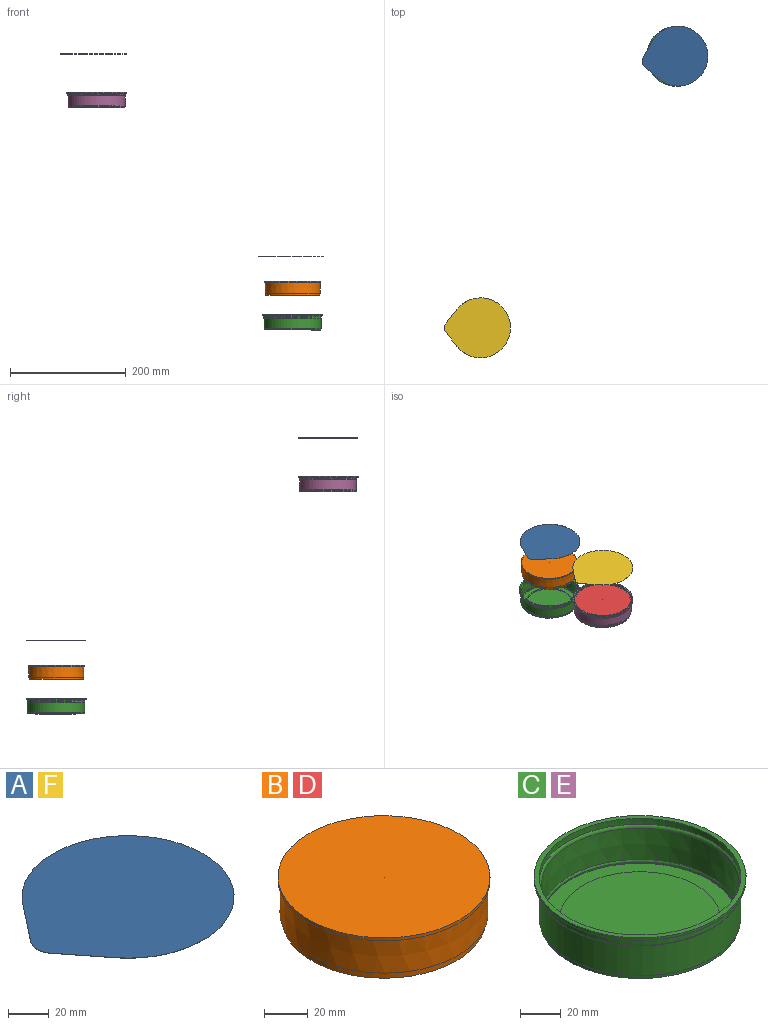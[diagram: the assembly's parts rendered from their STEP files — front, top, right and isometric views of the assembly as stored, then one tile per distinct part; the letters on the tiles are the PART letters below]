
ASSEMBLY  parts=6 mates=2
PART A: 6 faces, bbox 114.6x103.6x0.1 mm
  f0: cylinder r=51.77mm len=103.55mm, axis (0,0,-1), area 25.7mm2, adj f1,f3,f4,f5
  f1: plane 25.28x19.74mm, normal (-0.79,0.62,0), area 3.2mm2, adj f0,f2,f4,f5
  f2: cylinder r=10.71mm len=13.18mm, axis (0,0,-1), area 1.4mm2, adj f1,f3,f4,f5
  f3: plane 25.28x19.74mm, normal (-0.79,-0.62,0), area 3.2mm2, adj f0,f2,f4,f5
  f4: plane 114.59x103.55mm, normal (0,0,1), area 8724.1mm2, adj f0,f1,f2,f3
  f5: plane 114.59x103.55mm, normal (0,0,-1), area 8724.1mm2, adj f0,f1,f2,f3
PART B: 9 faces, bbox 97.3x97.3x24.2 mm
  f0: cone r=46.7mm half-angle=89.8deg, axis (0,0,1), area 2044.5mm2, adj f1,f8
  f1: cone r=46.69mm half-angle=0.2deg, axis (0,0,-1), area 1035.3mm2, adj f0,f2
  f2: cone r=47.71mm half-angle=89.8deg, axis (0,0,1), area 302.5mm2, adj f1,f3
  f3: cone r=47.66mm half-angle=0.2deg, axis (0,0,-1), area 5628.9mm2, adj f2,f4
  f4: cone r=48.63mm half-angle=89.8deg, axis (0,0,1), area 294.9mm2, adj f3,f5
  f5: cone r=48.63mm half-angle=0.2deg, axis (0,0,-1), area 506.3mm2, adj f4,f6
  f6: cone r=0mm half-angle=89.8deg, axis (0,0,1), area 7428.6mm2, adj f5
  f7: plane 78.22x78.22mm, normal (0,0,-1), area 4805.2mm2, adj f8
  f8: cone r=39.11mm half-angle=0.2deg, axis (0,0,-1), area 277.6mm2, adj f0,f7
PART C: 19 faces, bbox 108.9x108.9x26.8 mm
  f0: cylinder r=49.78mm len=99.55mm, axis (0,0,1), area 1376.1mm2, adj f1,f16
  f1: plane 103.55x103.55mm, normal (0,0,-1), area 638.1mm2, adj f0,f2
  f2: cylinder r=51.78mm len=103.55mm, axis (0,0,1), area 488mm2, adj f1,f3
  f3: cone r=37.5mm half-angle=89.9deg, axis (0,0,1), area 792mm2, adj f2,f10
  f4: plane 75x75mm, normal (0,0,-1), area 4417.7mm2, adj f5
  f5: cylinder r=37.5mm len=75mm, axis (0,0,1), area 235.6mm2, adj f4,f6
  f6: plane 97.55x97.55mm, normal (0,0,-1), area 3056.7mm2, adj f5,f7
  f7: cylinder r=48.78mm len=97.55mm, axis (0,0,1), area 612.9mm2, adj f6,f8
  f8: plane 98.55x98.55mm, normal (0,0,-1), area 154mm2, adj f7,f9
  f9: cylinder r=49.28mm len=98.55mm, axis (0,0,1), area 5573.1mm2, adj f8,f16
  f10: cone r=49.28mm half-angle=0.2deg, axis (0,0,-1), area 1040.9mm2, adj f3,f17
  f11: plane 78.22x78.22mm, normal (0,0,1), area 4805.2mm2, adj f12
  f12: cone r=39.11mm half-angle=0.2deg, axis (0,0,-1), area 277.6mm2, adj f11,f13
  f13: cone r=47.85mm half-angle=89.8deg, axis (0,0,1), area 2387.4mm2, adj f12,f14
  f14: cone r=47.85mm half-angle=0.2deg, axis (0,0,-1), area 203.6mm2, adj f13,f18
  f15: cone r=48.29mm half-angle=0.2deg, axis (0,0,-1), area 5642.6mm2, adj f17,f18
  f16: torus R=49.28mm, axis (0,0,-1), area 244.7mm2, adj f0,f9
  f17: torus R=50.3mm, axis (0,0,1), area 640.1mm2, adj f10,f15
  f18: torus R=49.85mm, axis (0,0,1), area 436.1mm2, adj f14,f15
PART D: same geometry as B
PART E: same geometry as C
PART F: same geometry as A
PLACE A rot(axis=(0,0.02,1),10.5deg) t=(337.73,471.44,-254.22)mm
PLACE B rot(axis=(0,0,1),10.5deg) t=(359.05,475.45,-322.06)mm
PLACE C rot(axis=(0,0,-1),79.5deg) t=(342.33,434.23,-380.67)mm
PLACE D t=(20.36,1.38,3.02)mm
PLACE E t=(34.14,1.38,3.6)mm
PLACE F rot(axis=(0,0,1),0deg) t=(-3.36,1.38,96.06)mm
MATE cylindrical A.f5 <-> C.f0  axis (0,0,-1) through (335.87,471.1,-254.22)mm
MATE cylindrical B.f6 <-> C.f0  axis (0,0,-1) through (335.67,471.1,-319.62)mm
